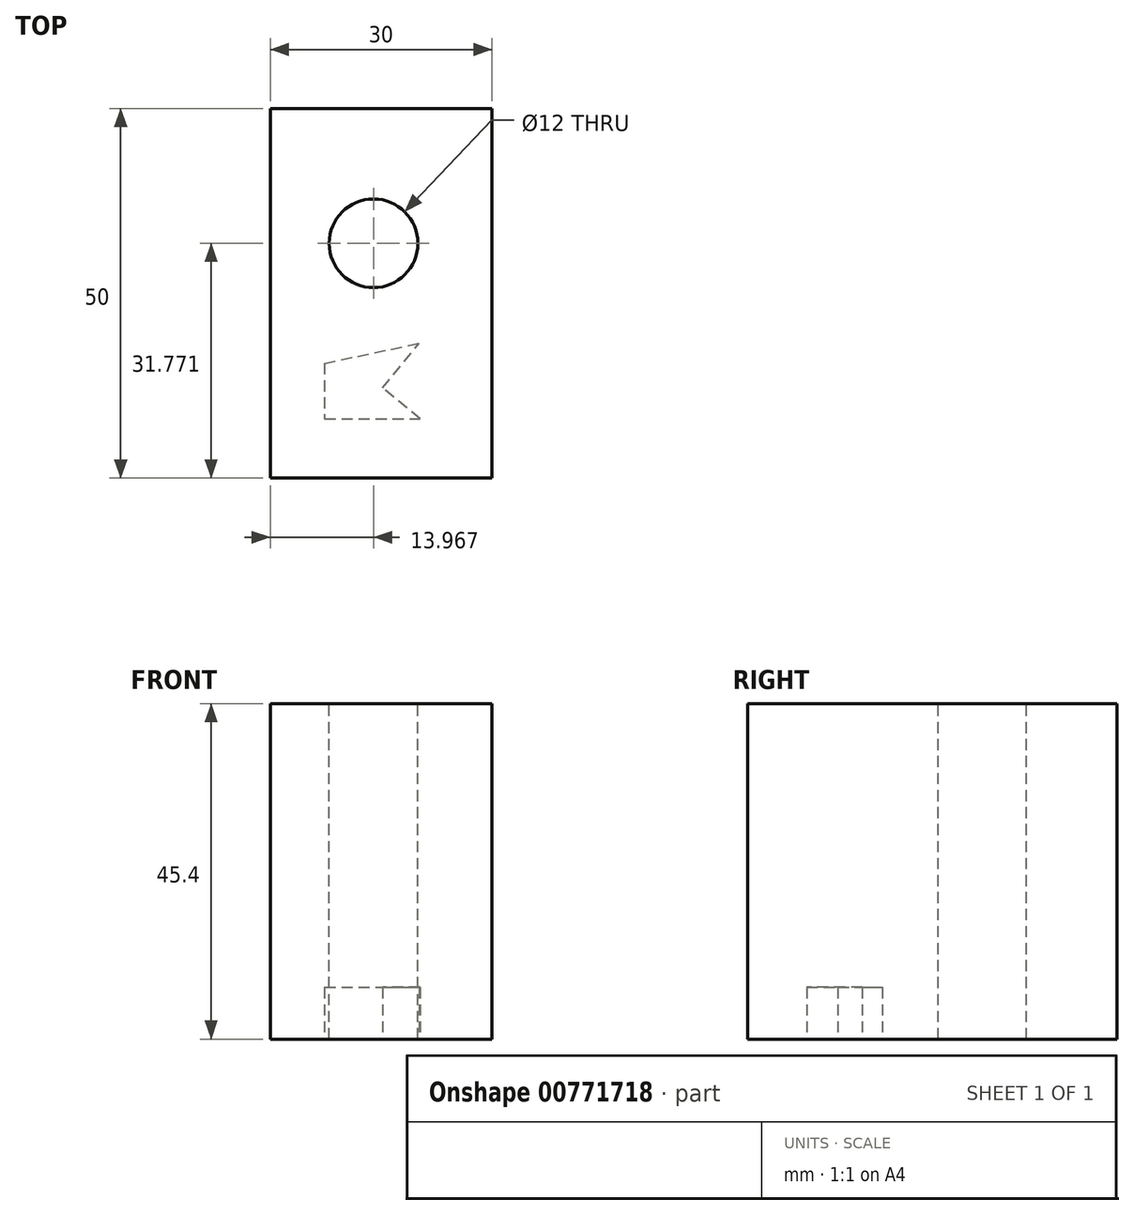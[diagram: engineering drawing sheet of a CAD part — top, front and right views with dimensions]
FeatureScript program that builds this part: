
annotation { "Feature Type Name" : "Feature", "Feature Type Description" : "" }
export const myFeature = defineFeature(function(context is Context, id is Id, definition is map)
    precondition{}
    {
        {
            var Q0;
            Q0=qCreatedBy(makeId("Top.planeOp"),FACE);
            var sketch = newSketch(context, id + "F0", { "sketchPlane" : qUnion([Q0])});
            skLineSegment(sketch, "E0.bottom", {"start": v(-37.88, 22.6) * mm, "end": v(-7.88, 22.6) * mm});
            skLineSegment(sketch, "E0.top", {"start": v(-37.88, -27.4) * mm, "end": v(-7.88, -27.4) * mm});
            skLineSegment(sketch, "E0.left", {"start": v(-37.88, 22.6) * mm, "end": v(-37.88, -27.4) * mm});
            skLineSegment(sketch, "E0.right", {"start": v(-7.88, 22.6) * mm, "end": v(-7.88, -27.4) * mm});
            skSolve(sketch);
        }
        {
            var Q0;
            Q0=makeQuery(id+"F0.imprint","IMPRINT",FACE,{"disambiguationData":[TD([[makeQuery(id+"F0.imprint","IMPRINT",EDGE,{"derivedFrom":sQuery(id+"F0.wireOp",EDGE,"E0.bottom")}),-1.0]])]});
            extrude(context, id + "F1", {"entities" : qUnion([Q0]), "depth" : 25.4 * mm, "offsetDistance" : 25.4 * mm});
        }
        {
            var Q0;
            Q0=makeQuery(id+"F1.opExtrude","CAP_FACE",FACE,{"disambiguationData":[OSD([sQuery(id+"F0.wireOp",EDGE,"E0.bottom"),sQuery(id+"F0.wireOp",EDGE,"E0.top"),sQuery(id+"F0.wireOp",EDGE,"E0.left"),sQuery(id+"F0.wireOp",EDGE,"E0.right")])],"isStart":false});
            extrude(context, id + "F2", {"entities" : qUnion([Q0]), "operationType" : NewBodyOperationType.ADD, "depth" : 20 * mm, "offsetDistance" : 25.4 * mm});
        }
        {
            var Q0;
            Q0=makeQuery(id+"F2.opExtrude","CAP_FACE",FACE,{"disambiguationData":[OSD([sQuery(id+"F0.wireOp",EDGE,"E0.bottom"),sQuery(id+"F0.wireOp",EDGE,"E0.top"),sQuery(id+"F0.wireOp",EDGE,"E0.left"),sQuery(id+"F0.wireOp",EDGE,"E0.right")])],"isStart":false});
            var sketch = newSketch(context, id + "F3", { "sketchPlane" : qUnion([Q0])});
            skPoint(sketch, "E1", {"position": v(-23.91, 4.36) * mm});
            skSolve(sketch);
        }
        {
            var Q0;
            Q0=sQuery(id+"F3.wireOp",VERTEX,"E1");
            var Q1;
            Q1=makeQuery(id+"F1.opExtrude","SWEPT_BODY",BODY,{"disambiguationData":[OSD([sQuery(id+"F0.wireOp",EDGE,"E0.bottom"),sQuery(id+"F0.wireOp",EDGE,"E0.top"),sQuery(id+"F0.wireOp",EDGE,"E0.left"),sQuery(id+"F0.wireOp",EDGE,"E0.right")])]});
            hole(context, id + "F4", {"style" : HoleStyle.SIMPLE, "endStyle" : HoleEndStyle.THROUGH, "holeDiameter" : 12 * mm, "majorDiameter" : 6.35 * mm, "isTappedThrough" : true, "tappedDepth" : 12.7 * mm, "tapClearance" : 3, "locations" : qUnion([Q0]), "scope" : qUnion([Q1])});
        }
        {
            var Q0;
            Q0=qCreatedBy(makeId("Top.planeOp"),FACE);
            var sketch = newSketch(context, id + "F5", { "sketchPlane" : qUnion([Q0])});
            skLineSegment(sketch, "E2", {"start": v(-30.53, -11.88) * mm, "end": v(-30.53, -19.4) * mm});
            skLineSegment(sketch, "E3", {"start": v(-30.53, -19.4) * mm, "end": v(-22.7, -19.4) * mm});
            skLineSegment(sketch, "E4", {"start": v(-22.7, -19.4) * mm, "end": v(-17.6, -19.4) * mm});
            skLineSegment(sketch, "E5", {"start": v(-17.6, -19.4) * mm, "end": v(-22.7, -15.19) * mm});
            skLineSegment(sketch, "E6", {"start": v(-22.7, -15.19) * mm, "end": v(-17.76, -9.17) * mm});
            skLineSegment(sketch, "E7", {"start": v(-30.53, -11.88) * mm, "end": v(-17.76, -9.17) * mm});
            skSolve(sketch);
        }
        {
            var Q0;
            Q0=makeQuery(id+"F5.imprint","IMPRINT",FACE,{"disambiguationData":[TD([[makeQuery(id+"F5.imprint","IMPRINT",EDGE,{"derivedFrom":sQuery(id+"F5.wireOp",EDGE,"E2")}),1.0]])]});
            extrude(context, id + "F6", {"entities" : qUnion([Q0]), "operationType" : NewBodyOperationType.REMOVE, "depth" : 7 * mm, "offsetDistance" : 25.4 * mm});
        }
    });
